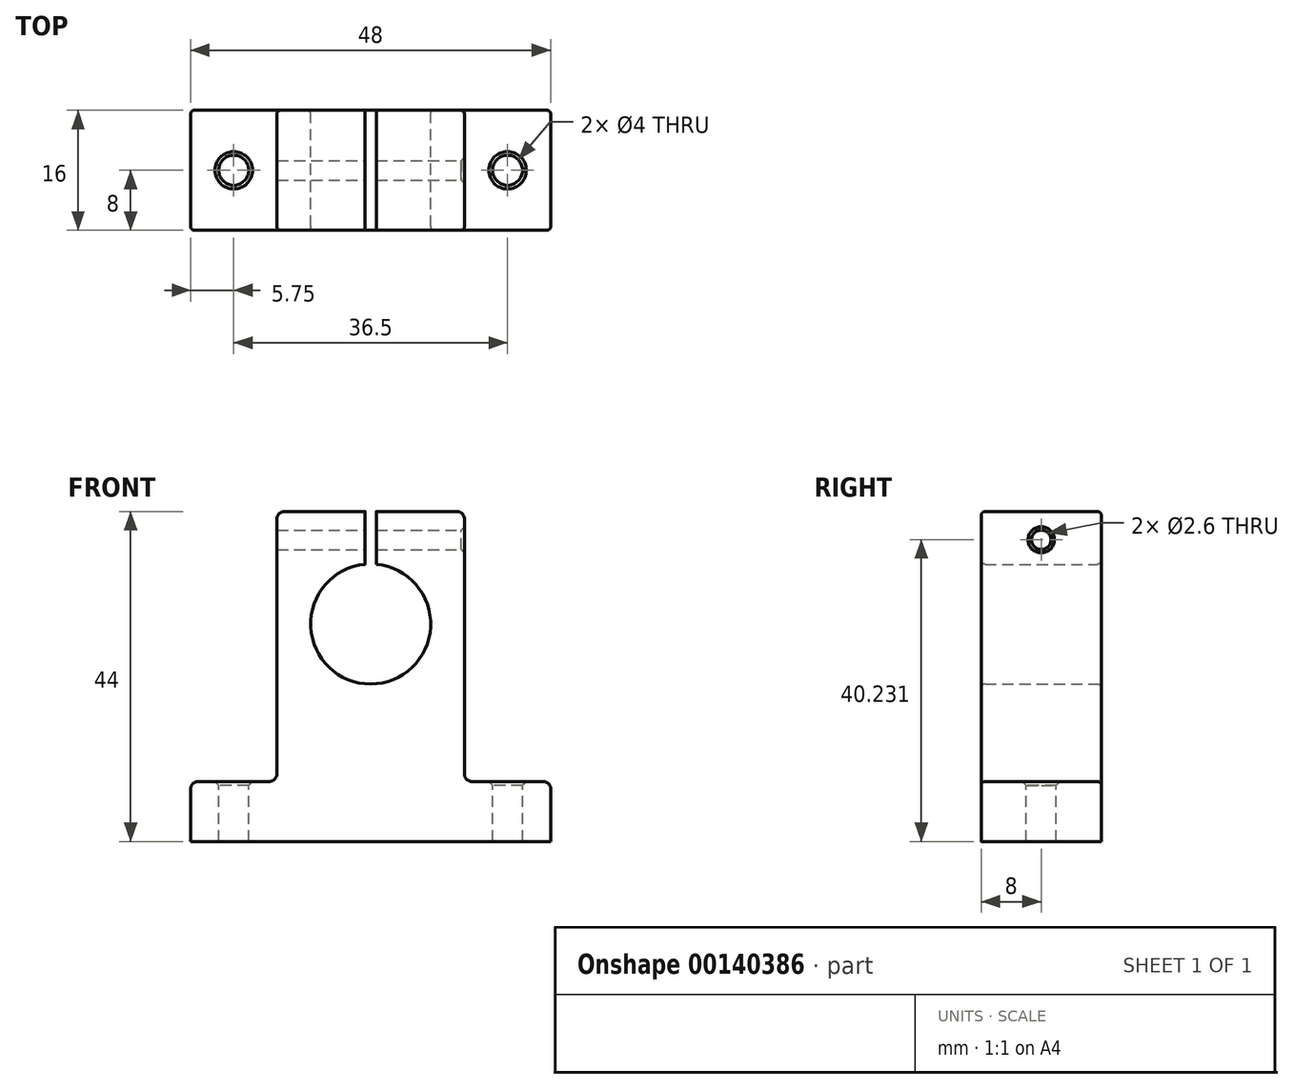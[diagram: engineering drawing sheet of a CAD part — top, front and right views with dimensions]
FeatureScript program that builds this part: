
annotation { "Feature Type Name" : "Feature", "Feature Type Description" : "" }
export const myFeature = defineFeature(function(context is Context, id is Id, definition is map)
    precondition{}
    {
        {
            var Q0;
            Q0=qCreatedBy(makeId("Front.planeOp"),FACE);
            var sketch = newSketch(context, id + "F0", { "sketchPlane" : qUnion([Q0])});
            skLineSegment(sketch, "E0", {"start": v(24, -18.9) * mm, "end": v(-24, -18.9) * mm});
            skLineSegment(sketch, "E1", {"start": v(-24, -18.9) * mm, "end": v(-24, -11.9) * mm});
            skLineSegment(sketch, "E2", {"start": v(-23, -10.9) * mm, "end": v(-13.5, -10.9) * mm});
            skLineSegment(sketch, "E3", {"start": v(-12.5, -9.9) * mm, "end": v(-12.5, 24.1) * mm});
            skLineSegment(sketch, "E4", {"start": v(-11.5, 25.1) * mm, "end": v(-0.75, 25.1) * mm});
            skLineSegment(sketch, "E5", {"start": v(12.5, 24.1) * mm, "end": v(12.5, -9.9) * mm});
            skLineSegment(sketch, "E6", {"start": v(13.5, -10.9) * mm, "end": v(23, -10.9) * mm});
            skLineSegment(sketch, "E7", {"start": v(24, -11.9) * mm, "end": v(24, -18.9) * mm});
            skLineSegment(sketch, "E8", {"start": v(0, 21.92) * mm, "end": v(0, -13.78) * mm, "construction": true});
            skPoint(sketch, "E9.visualSharp", {"position": v(-12.5, 25.1) * mm});
            skArc(sketch, "E9.filletArc", {"start": v(-11.5, 25.1) * mm, "mid": v(-12.2, 24.82) * mm, "end": v(-12.5, 24.1) * mm});
            skPoint(sketch, "E10.visualSharp", {"position": v(12.5, 25.1) * mm});
            skArc(sketch, "E10.filletArc", {"start": v(12.5, 24.1) * mm, "mid": v(12.2, 24.82) * mm, "end": v(11.5, 25.1) * mm});
            skPoint(sketch, "E11.visualSharp", {"position": v(12.5, -10.9) * mm});
            skArc(sketch, "E11.filletArc", {"start": v(12.5, -9.9) * mm, "mid": v(12.8, -10.6) * mm, "end": v(13.5, -10.9) * mm});
            skPoint(sketch, "E12.visualSharp", {"position": v(-12.5, -10.9) * mm});
            skArc(sketch, "E12.filletArc", {"start": v(-13.5, -10.9) * mm, "mid": v(-12.8, -10.6) * mm, "end": v(-12.5, -9.9) * mm});
            skPoint(sketch, "E13.visualSharp", {"position": v(24, -10.9) * mm});
            skArc(sketch, "E13.filletArc", {"start": v(24, -11.9) * mm, "mid": v(23.7, -11.18) * mm, "end": v(23, -10.9) * mm});
            skPoint(sketch, "E14.visualSharp", {"position": v(-24, -10.9) * mm});
            skArc(sketch, "E14.filletArc", {"start": v(-23, -10.9) * mm, "mid": v(-23.7, -11.18) * mm, "end": v(-24, -11.9) * mm});
            skArc(sketch, "E15", {"start": v(-0.75, 18.07) * mm, "mid": v(0, 2.1) * mm, "end": v(0.75, 18.07) * mm});
            skLineSegment(sketch, "E16", {"start": v(-0.75, 25.1) * mm, "end": v(-0.75, 18.07) * mm});
            skLineSegment(sketch, "E17.MirrorCS", {"start": v(0.75, 25.1) * mm, "end": v(0.75, 18.07) * mm});
            skPoint(sketch, "E18.orphan", {"position": v(-0.75, 28.9) * mm});
            skPoint(sketch, "E19.orphan", {"position": v(0.75, 28.9) * mm});
            skLineSegment(sketch, "E20.trimOffspring", {"start": v(0.75, 25.1) * mm, "end": v(11.5, 25.1) * mm});
            skPoint(sketch, "E21.orphan", {"position": v(0.75, 12.73) * mm});
            skPoint(sketch, "E22.orphan", {"position": v(-0.75, 12.73) * mm});
            skSolve(sketch);
        }
        {
            var Q0;
            Q0 = qSketchRegion(id + "F0", true);
            extrude(context, id + "F1", {"entities" : qUnion([Q0]), "endBound" : BoundingType.SYMMETRIC, "depth" : 16 * mm});
        }
        {
            var Q0;
            Q0=makeQuery(id+"F1.opExtrude","CAP_EDGE",EDGE,{"disambiguationData":[OSD([sQuery(id+"F0.wireOp",EDGE,"E5")])],"isStart":false});
            var Q1;
            Q1=makeQuery(id+"F1.opExtrude","CAP_EDGE",EDGE,{"disambiguationData":[OSD([sQuery(id+"F0.wireOp",EDGE,"E3")])],"isStart":false});
            var Q2;
            Q2=makeQuery(id+"F1.opExtrude","CAP_EDGE",EDGE,{"disambiguationData":[OSD([sQuery(id+"F0.wireOp",EDGE,"E3")])],"isStart":true});
            var Q3;
            Q3=makeQuery(id+"F1.opExtrude","CAP_EDGE",EDGE,{"disambiguationData":[OSD([sQuery(id+"F0.wireOp",EDGE,"E5")])],"isStart":true});
            fillet(context, id + "F2", {"entities" : qUnion([Q0, Q1, Q2, Q3]), "radius" : 0.5 * mm, "tangentPropagation" : true, "allowEdgeOverflow" : false});
        }
        {
            var Q0;
            Q0=makeQuery(id+"F1.opExtrude","CAP_EDGE",EDGE,{"disambiguationData":[OSD([sQuery(id+"F0.wireOp",EDGE,"E15")])],"isStart":false});
            var Q1;
            Q1=makeQuery(id+"F1.opExtrude","CAP_EDGE",EDGE,{"disambiguationData":[OSD([sQuery(id+"F0.wireOp",EDGE,"E15")])],"isStart":true});
            fillet(context, id + "F3", {"entities" : qUnion([Q0, Q1]), "radius" : 0.5 * mm, "tangentPropagation" : true, "allowEdgeOverflow" : false});
        }
        {
            var Q0;
            Q0=makeQuery(id+"F1.opExtrude","SWEPT_FACE",FACE,{"disambiguationData":[OSD([sQuery(id+"F0.wireOp",EDGE,"E6")])]});
            var sketch = newSketch(context, id + "F4", { "sketchPlane" : qUnion([Q0])});
            skPoint(sketch, "E23", {"position": v(18.25, 0) * mm});
            skLineSegment(sketch, "E24.0.1", {"start": v(8, -7.5) * mm, "end": v(-8, -7.5) * mm});
            skPoint(sketch, "E24.1", {"position": v(0, 8) * mm});
            skLineSegment(sketch, "E25", {"start": v(0, 8) * mm, "end": v(0, -8.85) * mm, "construction": true});
            skPoint(sketch, "E25.endSnap0", {"position": v(0, -7.5) * mm});
            skPoint(sketch, "E26", {"position": v(-18.25, 0) * mm});
            skSolve(sketch);
        }
        {
            var Q0;
            Q0=sQuery(id+"F4.wireOp",VERTEX,"E26");
            var Q1;
            Q1=sQuery(id+"F4.wireOp",VERTEX,"E23");
            var Q2;
            Q2=makeQuery(id+"F1.opExtrude","SWEPT_BODY",BODY,{"disambiguationData":[OSD([sQuery(id+"F0.wireOp",EDGE,"E0"),sQuery(id+"F0.wireOp",EDGE,"E1"),sQuery(id+"F0.wireOp",EDGE,"E2"),sQuery(id+"F0.wireOp",EDGE,"E3"),sQuery(id+"F0.wireOp",EDGE,"E4"),sQuery(id+"F0.wireOp",EDGE,"E5"),sQuery(id+"F0.wireOp",EDGE,"E6"),sQuery(id+"F0.wireOp",EDGE,"E7"),sQuery(id+"F0.wireOp",EDGE,"E9.filletArc"),sQuery(id+"F0.wireOp",EDGE,"E10.filletArc"),sQuery(id+"F0.wireOp",EDGE,"E11.filletArc"),sQuery(id+"F0.wireOp",EDGE,"E12.filletArc"),sQuery(id+"F0.wireOp",EDGE,"E13.filletArc"),sQuery(id+"F0.wireOp",EDGE,"E14.filletArc"),sQuery(id+"F0.wireOp",EDGE,"E15"),sQuery(id+"F0.wireOp",EDGE,"E16"),sQuery(id+"F0.wireOp",EDGE,"E17.MirrorCS"),sQuery(id+"F0.wireOp",EDGE,"E20.trimOffspring")])]});
            hole(context, id + "F5", {"style" : HoleStyle.C_SINK, "endStyle" : HoleEndStyle.THROUGH, "holeDiameter" : 4 * mm, "cSinkDiameter" : 5 * mm, "cSinkAngle" : 90 * degree, "majorDiameter" : 5 * mm, "isTappedThrough" : true, "tappedDepth" : 12 * mm, "tapClearance" : 3, "locations" : qUnion([Q0, Q1]), "scope" : qUnion([Q2])});
        }
        {
            var Q0;
            Q0=makeQuery(id+"F1.opExtrude","SWEPT_FACE",FACE,{"disambiguationData":[OSD([sQuery(id+"F0.wireOp",EDGE,"E5")])]});
            var sketch = newSketch(context, id + "F6", { "sketchPlane" : qUnion([Q0])});
            skPoint(sketch, "E27", {"position": v(0, 21.34) * mm});
            skSolve(sketch);
        }
        {
            var Q0;
            Q0=sQuery(id+"F6.wireOp",VERTEX,"E27");
            var Q1;
            Q1=makeQuery(id+"F1.opExtrude","SWEPT_BODY",BODY,{"disambiguationData":[OSD([sQuery(id+"F0.wireOp",EDGE,"E0"),sQuery(id+"F0.wireOp",EDGE,"E1"),sQuery(id+"F0.wireOp",EDGE,"E2"),sQuery(id+"F0.wireOp",EDGE,"E3"),sQuery(id+"F0.wireOp",EDGE,"E4"),sQuery(id+"F0.wireOp",EDGE,"E5"),sQuery(id+"F0.wireOp",EDGE,"E6"),sQuery(id+"F0.wireOp",EDGE,"E7"),sQuery(id+"F0.wireOp",EDGE,"E9.filletArc"),sQuery(id+"F0.wireOp",EDGE,"E10.filletArc"),sQuery(id+"F0.wireOp",EDGE,"E11.filletArc"),sQuery(id+"F0.wireOp",EDGE,"E12.filletArc"),sQuery(id+"F0.wireOp",EDGE,"E13.filletArc"),sQuery(id+"F0.wireOp",EDGE,"E14.filletArc"),sQuery(id+"F0.wireOp",EDGE,"E15"),sQuery(id+"F0.wireOp",EDGE,"E16"),sQuery(id+"F0.wireOp",EDGE,"E17.MirrorCS"),sQuery(id+"F0.wireOp",EDGE,"E20.trimOffspring")])]});
            hole(context, id + "F7", {"style" : HoleStyle.C_SINK, "endStyle" : HoleEndStyle.THROUGH, "holeDiameter" : 2.6 * mm, "cSinkDiameter" : 3.5 * mm, "cSinkAngle" : 90 * degree, "majorDiameter" : 5 * mm, "isTappedThrough" : true, "tappedDepth" : 12 * mm, "tapClearance" : 3, "locations" : qUnion([Q0]), "scope" : qUnion([Q1])});
        }
    });
